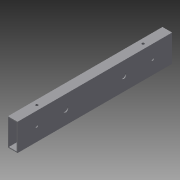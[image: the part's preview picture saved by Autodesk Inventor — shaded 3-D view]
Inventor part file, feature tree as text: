
AUTODESK INVENTOR PART (.ipt)
format: ipt  version: 2015 (Build 190159000, 159)  size: 112,640 bytes
history: native  units: in
note: dims shown in document units (in); Inventor stores cm internally (conversion verified against a paired STEP export)
features: sketch x4, hole x3, extrude x1, projected_geometry x1
ambient origin geometry x8: Origin, YZ Plane, XZ Plane, XY Plane, X Axis, Y Axis, Z Axis, Center Point
bodies: Solid1 (feature_tree)
feature tree (9):
  extrude  "Extrusion1"  Depth=0.5in
  hole  "Hole1"  [1 undecoded]
  hole  "Hole2"  [1 undecoded]
  hole  "Hole3"  [1 undecoded]
  sketch  "Sketch1"  dims[d0=1.4in d1=0.5in]
  sketch  "Sketch2"  dims[d2=0.05in d3=8.0in d4=0.0in]
  sketch  "Sketch3"  dims[d5=0.7in d6=1.0in]
  sketch  "Sketch4"  dims[d7=1.0in d11=0.1285in d12=0.75in d13=0.375in d14=0.25in d15=0.5635in d16=1.0in d17=0.8108in d18=1.5in d19=1.5in d20=0.257in d21=0.75in d22=0.375in d23=0.25in d24=0.5635in d25=1.0in d26=0.8108in d27=0.25in d28=1.25in d29=1.25in d30=0.128in d31=0.75in d32=0.375in d33=0.25in d34=0.5635in d35=1.0in d36=0.8108in]
  projected_geometry  "Projected Loop1"
note: 3 required parameter values undecoded (feature->parameter linkage not recoverable at this tier; creation-order binding heuristic only, values carry confidence <= 0.55)
